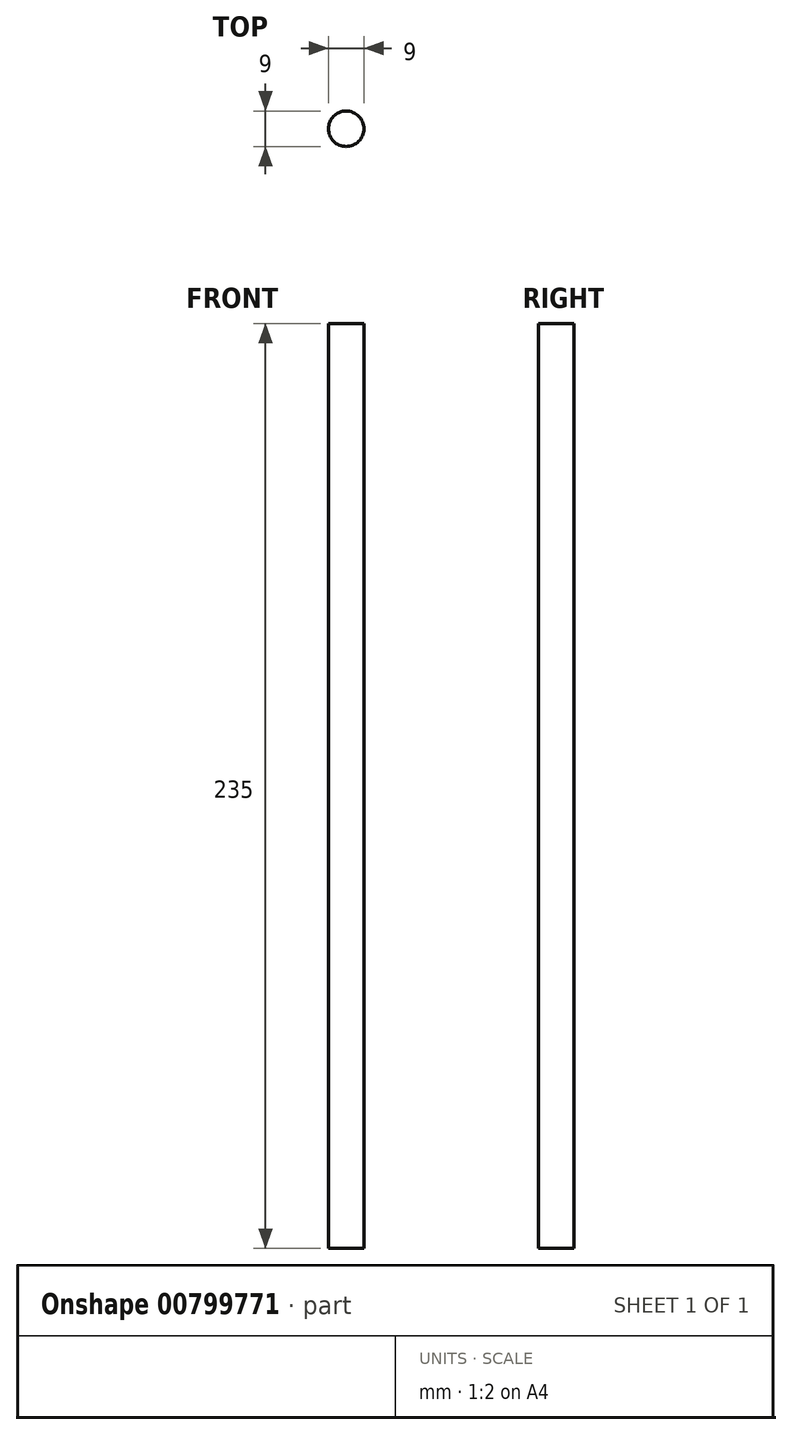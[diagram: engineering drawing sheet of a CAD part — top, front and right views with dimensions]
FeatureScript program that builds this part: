
annotation { "Feature Type Name" : "Feature", "Feature Type Description" : "" }
export const myFeature = defineFeature(function(context is Context, id is Id, definition is map)
    precondition{}
    {
        {
            var Q0;
            Q0=qCreatedBy(makeId("Top.planeOp"),FACE);
            var sketch = newSketch(context, id + "F0", { "sketchPlane" : qUnion([Q0])});
            skCircle(sketch, "E0", {"center": v(0, 0) * mm, "radius": 4.5 * mm});
            skSolve(sketch);
        }
        {
            var Q0;
            Q0=makeQuery(id+"F0.imprint","IMPRINT",FACE,{"disambiguationData":[TD([[makeQuery(id+"F0.imprint","IMPRINT",EDGE,{"derivedFrom":sQuery(id+"F0.wireOp",EDGE,"E0")}),1.0]])]});
            extrude(context, id + "F1", {"entities" : qUnion([Q0]), "depth" : 235 * mm, "offsetDistance" : 25 * mm});
        }
    });
